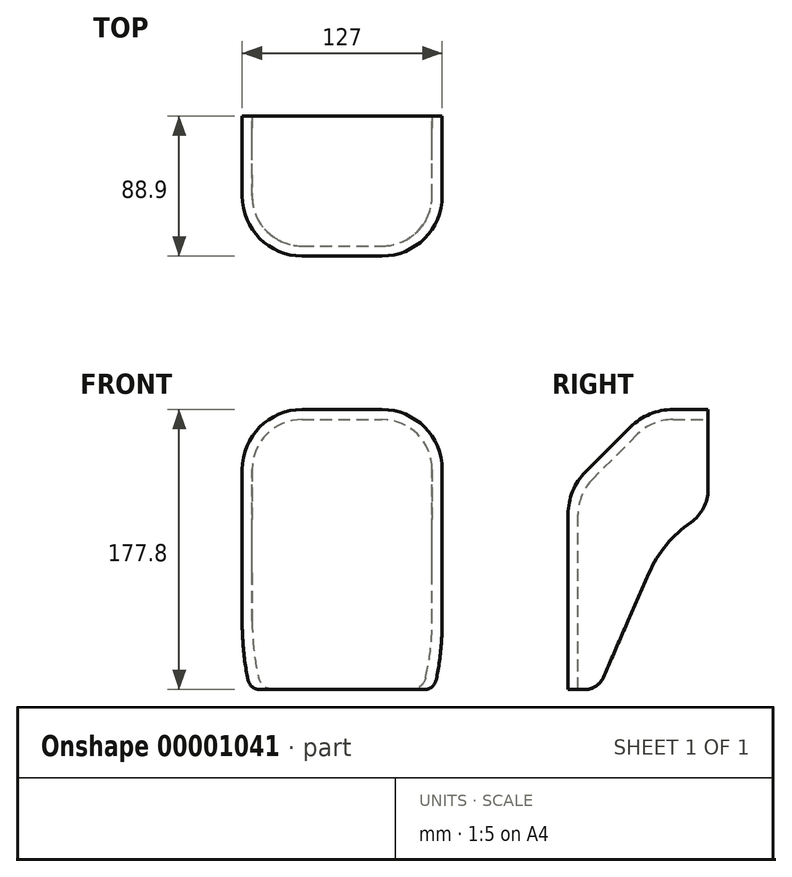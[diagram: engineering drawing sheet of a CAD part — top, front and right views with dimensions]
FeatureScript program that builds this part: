
annotation { "Feature Type Name" : "Feature", "Feature Type Description" : "" }
export const myFeature = defineFeature(function(context is Context, id is Id, definition is map)
    precondition{}
    {
        {
            var Q0;
            Q0=qCreatedBy(makeId("Top.planeOp"),FACE);
            var sketch = newSketch(context, id + "F0", { "sketchPlane" : qUnion([Q0])});
            skLineSegment(sketch, "E0", {"start": v(-63.5, -44.45) * mm, "end": v(63.5, -44.45) * mm});
            skLineSegment(sketch, "E1", {"start": v(63.5, -44.45) * mm, "end": v(63.5, 44.45) * mm});
            skLineSegment(sketch, "E2", {"start": v(-63.5, -44.45) * mm, "end": v(-63.5, 44.45) * mm});
            skLineSegment(sketch, "E3", {"start": v(-63.5, 44.45) * mm, "end": v(63.5, 44.45) * mm});
            skSolve(sketch);
        }
        {
            var Q0;
            Q0=makeQuery(id+"F0.imprint","IMPRINT",FACE,{"disambiguationData":[TD([[makeQuery(id+"F0.imprint","IMPRINT",EDGE,{"derivedFrom":sQuery(id+"F0.wireOp",EDGE,"E0")}),1.0]])]});
            extrude(context, id + "F1", {"entities" : qUnion([Q0]), "depth" : 76.2 * mm});
        }
        {
            var Q0;
            Q0=makeQuery(id+"F1.opExtrude","CAP_EDGE",EDGE,{"disambiguationData":[OSD([sQuery(id+"F0.wireOp",EDGE,"E0")])],"isStart":false});
            chamfer(context, id + "F2", {"entities" : qUnion([Q0]), "width" : 50.8 * mm, "tangentPropagation" : true});
        }
        {
            var Q0;
            Q0=makeQuery(id+"F2.opChamfer","BLEND_EDGE",EDGE,{"blendedFrom":[makeQuery(id+"F1.opExtrude","CAP_EDGE",EDGE,{"disambiguationData":[OSD([sQuery(id+"F0.wireOp",EDGE,"E0")])],"isStart":false}),makeQuery(id+"F1.opExtrude","SWEPT_FACE",FACE,{"disambiguationData":[OSD([sQuery(id+"F0.wireOp",EDGE,"E2")])]})],"blendedInto":[makeQuery(id+"F1.opExtrude","SWEPT_FACE",FACE,{"disambiguationData":[OSD([sQuery(id+"F0.wireOp",EDGE,"E2")])]})]});
            var Q1;
            Q1=makeQuery(id+"F1.opExtrude","CAP_EDGE",EDGE,{"disambiguationData":[OSD([sQuery(id+"F0.wireOp",EDGE,"E2")])],"isStart":false});
            var Q2;
            Q2=makeQuery(id+"F1.opExtrude","CAP_EDGE",EDGE,{"disambiguationData":[OSD([sQuery(id+"F0.wireOp",EDGE,"E1")])],"isStart":false});
            var Q3;
            Q3=makeQuery(id+"F2.opChamfer","BLEND_EDGE",EDGE,{"blendedFrom":[makeQuery(id+"F1.opExtrude","CAP_EDGE",EDGE,{"disambiguationData":[OSD([sQuery(id+"F0.wireOp",EDGE,"E0")])],"isStart":false}),makeQuery(id+"F1.opExtrude","SWEPT_FACE",FACE,{"disambiguationData":[OSD([sQuery(id+"F0.wireOp",EDGE,"E1")])]})],"blendedInto":[makeQuery(id+"F1.opExtrude","SWEPT_FACE",FACE,{"disambiguationData":[OSD([sQuery(id+"F0.wireOp",EDGE,"E1")])]})]});
            var Q4;
            Q4=makeQuery(id+"F1.opExtrude","SWEPT_EDGE",EDGE,{"disambiguationData":[OSD([sQuery(id+"F0.wireOp",EDGE,"E0"),sQuery(id+"F0.wireOp",EDGE,"E1")])]});
            var Q5;
            Q5=makeQuery(id+"F1.opExtrude","SWEPT_EDGE",EDGE,{"disambiguationData":[OSD([sQuery(id+"F0.wireOp",EDGE,"E0"),sQuery(id+"F0.wireOp",EDGE,"E2")])]});
            var Q6;
            {var subQ0=sQuery(id+"F0.wireOp",EDGE,"E0");Q6=makeQuery(id+"F2.opChamfer","BLEND_EDGE",EDGE,{"blendedFrom":[makeQuery(id+"F1.opExtrude","CAP_EDGE",EDGE,{"disambiguationData":[OSD([subQ0])],"isStart":false}),makeQuery(id+"F1.opExtrude","SWEPT_FACE",FACE,{"disambiguationData":[OSD([subQ0])]})],"blendedInto":[makeQuery(id+"F1.opExtrude","SWEPT_FACE",FACE,{"disambiguationData":[OSD([subQ0])]})]});}
            var Q7;
            {var subQ0=sQuery(id+"F0.wireOp",EDGE,"E0");Q7=makeQuery(id+"F2.opChamfer","BLEND_EDGE",EDGE,{"blendedFrom":[makeQuery(id+"F1.opExtrude","CAP_EDGE",EDGE,{"disambiguationData":[OSD([subQ0])],"isStart":false}),makeQuery(id+"F1.opExtrude","CAP_FACE",FACE,{"disambiguationData":[OSD([subQ0,sQuery(id+"F0.wireOp",EDGE,"E1"),sQuery(id+"F0.wireOp",EDGE,"E2"),sQuery(id+"F0.wireOp",EDGE,"E3")])],"isStart":false})],"blendedInto":[makeQuery(id+"F1.opExtrude","CAP_FACE",FACE,{"disambiguationData":[OSD([subQ0,sQuery(id+"F0.wireOp",EDGE,"E1"),sQuery(id+"F0.wireOp",EDGE,"E2"),sQuery(id+"F0.wireOp",EDGE,"E3")])],"isStart":false})]});}
            fillet(context, id + "F3", {"entities" : qUnion([Q0, Q1, Q2, Q3, Q4, Q5, Q6, Q7]), "radius" : 38.1 * mm, "tangentPropagation" : true, "allowEdgeOverflow" : false});
        }
        {
            var Q0;
            Q0=makeQuery(id+"F1.opExtrude","SWEPT_FACE",FACE,{"disambiguationData":[OSD([sQuery(id+"F0.wireOp",EDGE,"E3")])]});
            var Q1;
            Q1=makeQuery(id+"F1.opExtrude","CAP_FACE",FACE,{"disambiguationData":[OSD([sQuery(id+"F0.wireOp",EDGE,"E0"),sQuery(id+"F0.wireOp",EDGE,"E1"),sQuery(id+"F0.wireOp",EDGE,"E2"),sQuery(id+"F0.wireOp",EDGE,"E3")])],"isStart":true});
            shell(context, id + "F4", {"entities" : qUnion([Q0, Q1]), "thickness" : 6.35 * mm});
        }
        {
            var Q0;
            {var subQ0=sQuery(id+"F0.wireOp",EDGE,"E3");Q0=makeQuery(id+"F4.opShell","OFFSET_EDGE",EDGE,{"disambiguationData":[OSD([subQ0]),TDD([makeQuery(id+"F1.opExtrude","CAP_EDGE",EDGE,{"disambiguationData":[OSD([subQ0])],"isStart":true})])]});}
            var Q1;
            Q1=makeQuery(id+"F1.opExtrude","CAP_EDGE",EDGE,{"disambiguationData":[OSD([sQuery(id+"F0.wireOp",EDGE,"E3")])],"isStart":true});
            fillet(context, id + "F5", {"entities" : qUnion([Q0, Q1]), "radius" : 25.4 * mm, "tangentPropagation" : true, "allowEdgeOverflow" : false});
        }
        {
            var Q0;
            Q0=makeQuery(id+"F1.opExtrude","CAP_FACE",FACE,{"disambiguationData":[OSD([sQuery(id+"F0.wireOp",EDGE,"E0"),sQuery(id+"F0.wireOp",EDGE,"E1"),sQuery(id+"F0.wireOp",EDGE,"E2"),sQuery(id+"F0.wireOp",EDGE,"E3")])],"isStart":true});
            extrude(context, id + "F6", {"entities" : qUnion([Q0]), "operationType" : NewBodyOperationType.ADD, "depth" : 101.6 * mm});
        }
        {
            var Q0;
            {var subQ0=sQuery(id+"F0.wireOp",EDGE,"E0");var subQ1=sQuery(id+"F0.wireOp",EDGE,"E1");var subQ2=sQuery(id+"F0.wireOp",EDGE,"E2");var subQ3=sQuery(id+"F0.wireOp",EDGE,"E3");Q0=makeQuery(id+"F6.opExtrude","CAP_EDGE",EDGE,{"disambiguationData":[OSD([subQ0,subQ1,subQ2,subQ3]),TDD([makeQuery(id+"F5.opFillet","BLEND_EDGE",EDGE,{"blendedFrom":[makeQuery(id+"F4.opShell","OFFSET_EDGE",EDGE,{"disambiguationData":[OSD([subQ3]),TDD([makeQuery(id+"F1.opExtrude","CAP_EDGE",EDGE,{"disambiguationData":[OSD([subQ3])],"isStart":true})])]}),makeQuery(id+"F1.opExtrude","CAP_FACE",FACE,{"disambiguationData":[OSD([subQ0,subQ1,subQ2,subQ3])],"isStart":true})],"blendedInto":[makeQuery(id+"F1.opExtrude","CAP_FACE",FACE,{"disambiguationData":[OSD([subQ0,subQ1,subQ2,subQ3])],"isStart":true})]})])],"isStart":false});}
            var Q1;
            {var subQ0=sQuery(id+"F0.wireOp",EDGE,"E0");var subQ1=sQuery(id+"F0.wireOp",EDGE,"E1");var subQ2=sQuery(id+"F0.wireOp",EDGE,"E2");var subQ3=sQuery(id+"F0.wireOp",EDGE,"E3");Q1=makeQuery(id+"F6.opExtrude","CAP_EDGE",EDGE,{"disambiguationData":[OSD([subQ0,subQ1,subQ2,subQ3]),TDD([makeQuery(id+"F5.opFillet","BLEND_EDGE",EDGE,{"blendedFrom":[makeQuery(id+"F1.opExtrude","CAP_EDGE",EDGE,{"disambiguationData":[OSD([subQ3])],"isStart":true}),makeQuery(id+"F1.opExtrude","CAP_FACE",FACE,{"disambiguationData":[OSD([subQ0,subQ1,subQ2,subQ3])],"isStart":true})],"blendedInto":[makeQuery(id+"F1.opExtrude","CAP_FACE",FACE,{"disambiguationData":[OSD([subQ0,subQ1,subQ2,subQ3])],"isStart":true})]})])],"isStart":false});}
            chamfer(context, id + "F7", {"entities" : qUnion([Q0, Q1]), "chamferType" : ChamferType.TWO_OFFSETS, "width1" : 101.6 * mm, "oppositeDirection" : true, "width2" : 44.45 * mm, "tangentPropagation" : true});
        }
        {
            var Q0;
            {var subQ0=sQuery(id+"F0.wireOp",EDGE,"E0");var subQ1=sQuery(id+"F0.wireOp",EDGE,"E1");var subQ2=sQuery(id+"F0.wireOp",EDGE,"E2");var subQ3=sQuery(id+"F0.wireOp",EDGE,"E3");var subQ4=makeQuery(id+"F4.opShell","OFFSET_EDGE",EDGE,{"disambiguationData":[OSD([subQ3]),TDD([makeQuery(id+"F1.opExtrude","CAP_EDGE",EDGE,{"disambiguationData":[OSD([subQ3])],"isStart":true})])]});Q0=makeQuery(id+"F7.opChamfer","BLEND_EDGE",EDGE,{"blendedFrom":[makeQuery(id+"F6.opExtrude","CAP_EDGE",EDGE,{"disambiguationData":[OSD([subQ0,subQ1,subQ2,subQ3]),TDD([makeQuery(id+"F5.opFillet","BLEND_EDGE",EDGE,{"blendedFrom":[subQ4,makeQuery(id+"F1.opExtrude","CAP_FACE",FACE,{"disambiguationData":[OSD([subQ0,subQ1,subQ2,subQ3])],"isStart":true})],"blendedInto":[makeQuery(id+"F1.opExtrude","CAP_FACE",FACE,{"disambiguationData":[OSD([subQ0,subQ1,subQ2,subQ3])],"isStart":true})]})])],"isStart":false}),makeQuery(id+"F5.opFillet","BLEND_FACE",FACE,{"disambiguationData":[OSD([subQ3]),TDD([subQ4])]})],"blendedInto":[makeQuery(id+"F5.opFillet","BLEND_FACE",FACE,{"disambiguationData":[OSD([subQ3]),TDD([subQ4])]})]});}
            var Q1;
            {var subQ0=sQuery(id+"F0.wireOp",EDGE,"E0");var subQ1=sQuery(id+"F0.wireOp",EDGE,"E1");var subQ2=sQuery(id+"F0.wireOp",EDGE,"E2");var subQ3=sQuery(id+"F0.wireOp",EDGE,"E3");var subQ4=makeQuery(id+"F1.opExtrude","CAP_EDGE",EDGE,{"disambiguationData":[OSD([subQ3])],"isStart":true});Q1=makeQuery(id+"F7.opChamfer","BLEND_EDGE",EDGE,{"blendedFrom":[makeQuery(id+"F6.opExtrude","CAP_EDGE",EDGE,{"disambiguationData":[OSD([subQ0,subQ1,subQ2,subQ3]),TDD([makeQuery(id+"F5.opFillet","BLEND_EDGE",EDGE,{"blendedFrom":[subQ4,makeQuery(id+"F1.opExtrude","CAP_FACE",FACE,{"disambiguationData":[OSD([subQ0,subQ1,subQ2,subQ3])],"isStart":true})],"blendedInto":[makeQuery(id+"F1.opExtrude","CAP_FACE",FACE,{"disambiguationData":[OSD([subQ0,subQ1,subQ2,subQ3])],"isStart":true})]})])],"isStart":false}),makeQuery(id+"F5.opFillet","BLEND_FACE",FACE,{"disambiguationData":[OSD([subQ3]),TDD([subQ4])]})],"blendedInto":[makeQuery(id+"F5.opFillet","BLEND_FACE",FACE,{"disambiguationData":[OSD([subQ3]),TDD([subQ4])]})]});}
            fillet(context, id + "F8", {"entities" : qUnion([Q0, Q1]), "radius" : 76.2 * mm, "tangentPropagation" : true, "allowEdgeOverflow" : false});
        }
        {
            var Q0;
            {var subQ0=sQuery(id+"F0.wireOp",EDGE,"E0");var subQ1=sQuery(id+"F0.wireOp",EDGE,"E1");var subQ2=sQuery(id+"F0.wireOp",EDGE,"E2");var subQ3=sQuery(id+"F0.wireOp",EDGE,"E3");Q0=makeQuery(id+"F7.opChamfer","BLEND_EDGE",EDGE,{"blendedFrom":[makeQuery(id+"F6.opExtrude","CAP_EDGE",EDGE,{"disambiguationData":[OSD([subQ0,subQ1,subQ2,subQ3]),TDD([makeQuery(id+"F5.opFillet","BLEND_EDGE",EDGE,{"blendedFrom":[makeQuery(id+"F4.opShell","OFFSET_EDGE",EDGE,{"disambiguationData":[OSD([subQ3]),TDD([makeQuery(id+"F1.opExtrude","CAP_EDGE",EDGE,{"disambiguationData":[OSD([subQ3])],"isStart":true})])]}),makeQuery(id+"F1.opExtrude","CAP_FACE",FACE,{"disambiguationData":[OSD([subQ0,subQ1,subQ2,subQ3])],"isStart":true})],"blendedInto":[makeQuery(id+"F1.opExtrude","CAP_FACE",FACE,{"disambiguationData":[OSD([subQ0,subQ1,subQ2,subQ3])],"isStart":true})]})])],"isStart":false}),makeQuery(id+"F6.opExtrude","CAP_FACE",FACE,{"disambiguationData":[OSD([subQ0,subQ1,subQ2,subQ3])],"isStart":false})],"blendedInto":[makeQuery(id+"F6.opExtrude","CAP_FACE",FACE,{"disambiguationData":[OSD([subQ0,subQ1,subQ2,subQ3])],"isStart":false})]});}
            var Q1;
            {var subQ0=sQuery(id+"F0.wireOp",EDGE,"E0");var subQ1=sQuery(id+"F0.wireOp",EDGE,"E1");var subQ2=sQuery(id+"F0.wireOp",EDGE,"E2");var subQ3=sQuery(id+"F0.wireOp",EDGE,"E3");Q1=makeQuery(id+"F7.opChamfer","BLEND_EDGE",EDGE,{"blendedFrom":[makeQuery(id+"F6.opExtrude","CAP_EDGE",EDGE,{"disambiguationData":[OSD([subQ0,subQ1,subQ2,subQ3]),TDD([makeQuery(id+"F5.opFillet","BLEND_EDGE",EDGE,{"blendedFrom":[makeQuery(id+"F1.opExtrude","CAP_EDGE",EDGE,{"disambiguationData":[OSD([subQ3])],"isStart":true}),makeQuery(id+"F1.opExtrude","CAP_FACE",FACE,{"disambiguationData":[OSD([subQ0,subQ1,subQ2,subQ3])],"isStart":true})],"blendedInto":[makeQuery(id+"F1.opExtrude","CAP_FACE",FACE,{"disambiguationData":[OSD([subQ0,subQ1,subQ2,subQ3])],"isStart":true})]})])],"isStart":false}),makeQuery(id+"F6.opExtrude","CAP_FACE",FACE,{"disambiguationData":[OSD([subQ0,subQ1,subQ2,subQ3])],"isStart":false})],"blendedInto":[makeQuery(id+"F6.opExtrude","CAP_FACE",FACE,{"disambiguationData":[OSD([subQ0,subQ1,subQ2,subQ3])],"isStart":false})]});}
            fillet(context, id + "F9", {"entities" : qUnion([Q0, Q1]), "radius" : 12.7 * mm, "tangentPropagation" : true, "allowEdgeOverflow" : false});
        }
    });
